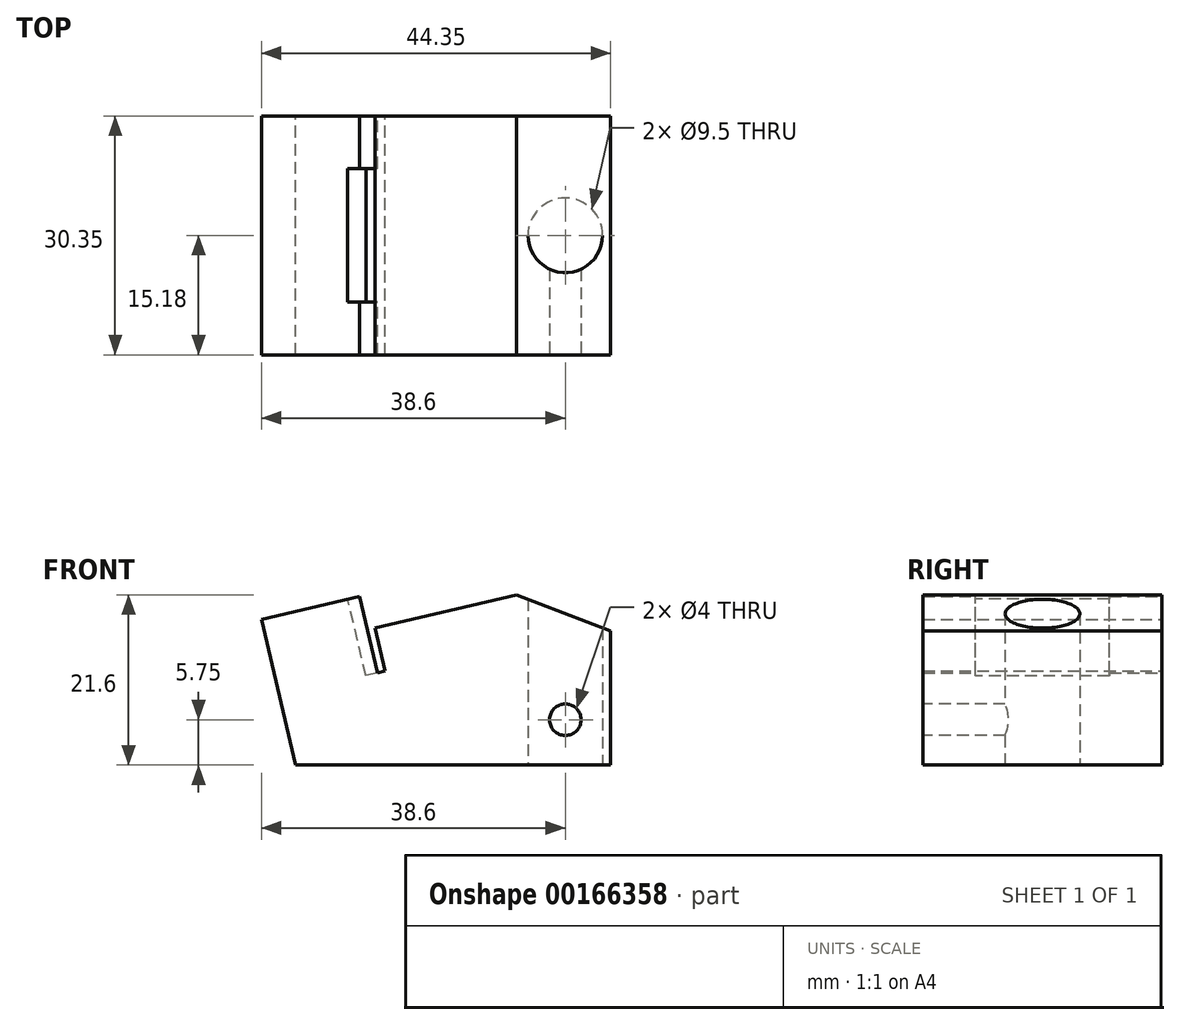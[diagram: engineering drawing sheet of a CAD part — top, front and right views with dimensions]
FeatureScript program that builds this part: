
annotation { "Feature Type Name" : "Feature", "Feature Type Description" : "" }
export const myFeature = defineFeature(function(context is Context, id is Id, definition is map)
    precondition{}
    {
        {
            var Q0;
            Q0=qCreatedBy(makeId("Front.planeOp"),FACE);
            var sketch = newSketch(context, id + "F0", { "sketchPlane" : qUnion([Q0])});
            skLineSegment(sketch, "E0", {"start": v(20, 0) * mm, "end": v(20, 17) * mm});
            skLineSegment(sketch, "E1", {"start": v(20, 17) * mm, "end": v(8.04, 21.6) * mm});
            skLineSegment(sketch, "E2", {"start": v(8.04, 21.6) * mm, "end": v(-9.9, 17.38) * mm});
            skLineSegment(sketch, "E3", {"start": v(-11.88, 21.43) * mm, "end": v(-24.35, 18.5) * mm});
            skLineSegment(sketch, "E4", {"start": v(-24.35, 18.5) * mm, "end": v(-20, 0) * mm});
            skLineSegment(sketch, "E5", {"start": v(-20, 0) * mm, "end": v(20, 0) * mm});
            skLineSegment(sketch, "E6", {"start": v(-9.9, 17.38) * mm, "end": v(-8.62, 11.92) * mm});
            skLineSegment(sketch, "E7", {"start": v(-8.62, 11.92) * mm, "end": v(-9.6, 11.7) * mm});
            skLineSegment(sketch, "E8", {"start": v(-9.6, 11.7) * mm, "end": v(-11.88, 21.43) * mm});
            skSolve(sketch);
        }
        {
            var Q0;
            Q0 = qSketchRegion(id + "F0", true);
            extrude(context, id + "F1", {"entities" : qUnion([Q0]), "endBound" : BoundingType.SYMMETRIC, "depth" : 30.35 * mm});
        }
        {
            var Q0;
            Q0=makeQuery(id+"F1.opExtrude","SWEPT_FACE",FACE,{"disambiguationData":[OSD([sQuery(id+"F0.wireOp",EDGE,"E5")])]});
            var sketch = newSketch(context, id + "F2", { "sketchPlane" : qUnion([Q0])});
            skLineSegment(sketch, "E9", {"start": v(-20, 0) * mm, "end": v(20, 0) * mm, "construction": true});
            skCircle(sketch, "E10", {"center": v(14.25, 0) * mm, "radius": 4.75 * mm});
            skSolve(sketch);
        }
        {
            var Q0;
            Q0 = qSketchRegion(id + "F2", true);
            extrude(context, id + "F3", {"entities" : qUnion([Q0]), "operationType" : NewBodyOperationType.REMOVE, "endBound" : BoundingType.THROUGH_ALL, "oppositeDirection" : true, "depth" : 25 * mm});
        }
        {
            var Q0;
            Q0=makeQuery(id+"F1.opExtrude","SWEPT_FACE",FACE,{"disambiguationData":[OSD([sQuery(id+"F0.wireOp",EDGE,"E3")])]});
            var sketch = newSketch(context, id + "F4", { "sketchPlane" : qUnion([Q0])});
            skLineSegment(sketch, "E11", {"start": v(-6.66, 8.5) * mm, "end": v(-8.2, 8.5) * mm});
            skLineSegment(sketch, "E12", {"start": v(-8.2, 8.5) * mm, "end": v(-8.2, -8.5) * mm});
            skLineSegment(sketch, "E13", {"start": v(-8.2, -8.5) * mm, "end": v(-6.66, -8.5) * mm});
            skLineSegment(sketch, "E14", {"start": v(-6.66, 8.5) * mm, "end": v(-6.66, 15.18) * mm, "construction": true});
            skLineSegment(sketch, "E15", {"start": v(-6.66, -8.5) * mm, "end": v(-6.66, -15.18) * mm, "construction": true});
            skLineSegment(sketch, "E16", {"start": v(-6.66, 8.5) * mm, "end": v(-6.66, -8.5) * mm});
            skSolve(sketch);
        }
        {
            var Q0;
            Q0=makeQuery(id+"F4.imprint","IMPRINT",FACE,{"disambiguationData":[TD([[makeQuery(id+"F4.imprint","IMPRINT",EDGE,{"derivedFrom":sQuery(id+"F4.wireOp",EDGE,"E11")}),1.0]])]});
            extrude(context, id + "F5", {"entities" : qUnion([Q0]), "operationType" : NewBodyOperationType.REMOVE, "oppositeDirection" : true, "depth" : 10 * mm});
        }
        {
            var Q0;
            Q0=makeQuery(id+"F1.opExtrude","CAP_FACE",FACE,{"disambiguationData":[OSD([sQuery(id+"F0.wireOp",EDGE,"E0"),sQuery(id+"F0.wireOp",EDGE,"E1"),sQuery(id+"F0.wireOp",EDGE,"E2"),sQuery(id+"F0.wireOp",EDGE,"FyUAAAzV-o3TN-1j9J-W0mW-qlrIonVJf6ou"),sQuery(id+"F0.wireOp",EDGE,"XsSguIEQ-URj3-VmBn-xh4o-mCVxJUMvp43w"),sQuery(id+"F0.wireOp",EDGE,"gGLLkclF-o3c9-q1If-ihrD-o2IAE7qHNqVM"),sQuery(id+"F0.wireOp",EDGE,"E3"),sQuery(id+"F0.wireOp",EDGE,"E4"),sQuery(id+"F0.wireOp",EDGE,"E5")])],"isStart":false});
            var sketch = newSketch(context, id + "F6", { "sketchPlane" : qUnion([Q0])});
            skCircle(sketch, "E17", {"center": v(14.25, 5.75) * mm, "radius": 2 * mm});
            skSolve(sketch);
        }
        {
            var Q0;
            Q0 = qSketchRegion(id + "F6", true);
            extrude(context, id + "F7", {"entities" : qUnion([Q0]), "operationType" : NewBodyOperationType.REMOVE, "endBound" : BoundingType.UP_TO_NEXT, "oppositeDirection" : true, "depth" : 25 * mm});
        }
    });
